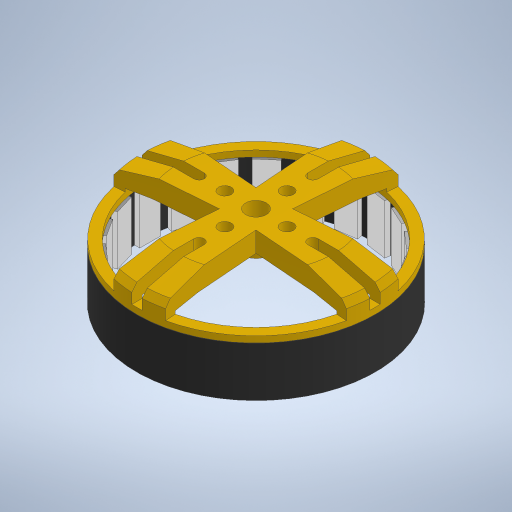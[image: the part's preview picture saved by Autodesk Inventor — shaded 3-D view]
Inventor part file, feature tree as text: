
AUTODESK INVENTOR PART (.ipt)
format: ipt  version: 2023.1 (Build 271208000, 208)  size: 626,176 bytes
history: native  units: in
note: dims shown in document units (in); Inventor stores cm internally (conversion verified against a paired STEP export)
features: sketch x4, extrude x3, chamfer x2, revolve x1
ambient origin geometry x8: Origin, YZ Plane, XZ Plane, XY Plane, X Axis, Y Axis, Z Axis, Center Point
bodies: Solid1 (feature_tree)
feature tree (10):
  extrude  "Extrusion1"  Depth=0.0591in
  extrude  "Extrusion2"  Depth=0.0394in
  revolve  "Revolution1"  Angle=360.0deg
  chamfer  "Chamfer1"  Distance=0.378in
  chamfer  "Chamfer2"  Distance=0.9055in
  extrude  "Extrusion4"  Depth=0.3937in
  sketch  "Sketch1"  dims[d0=1.815in d1=0.0591in]
  sketch  "Sketch2"  dims[d2=0.378in d3=0.0in d4=0.0394in]
  sketch  "Sketch4"  dims[d5=0.1575in d6=8.6614in d8=360.0deg d10=0.378in d11=0.0in]
  sketch  "Sketch5"  dims[d15=0.2441in d16=0.9055in d17=0.0906in d18=0.8268in d19=0.0709in d20=0.185in d21=360.0deg d22=0.315in d23=0.0787in d24=45.0deg d25=0.0394in d26=0.0787in d27=45.0deg d28=0.1181in d29=0.1476in d30=0.0787in d31=0.4724in d32=0.0984in d33=1.5748in d35=360.0deg d37=0.0787in d38=0.7874in d39=1.5748in d41=360.0deg d43=45.0deg d44=0.3937in d45=0.1969in d46=0.1476in d47=1.5748in d49=360.0deg d51=0.1969in d52=0.0in]
